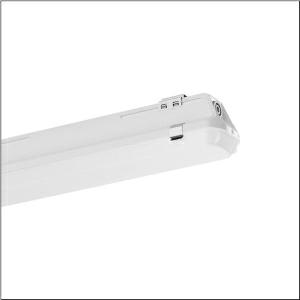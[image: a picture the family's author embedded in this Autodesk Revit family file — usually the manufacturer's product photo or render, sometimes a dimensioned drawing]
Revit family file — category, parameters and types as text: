
# Revit family: monsun_r__11_51fp20dp460h_2810
name_source: partatom
category: Lighting Fixtures
units: mm (PartAtom-declared; Revit-internal decimal feet)

## family parameters
Cut with Voids When Loaded = No
Host = Face
Light Source = No
Part Type = Normal
Room Calculation Point = No
Round Connector Dimension = Use Diameter
Shared = No

## types (1)
- --- (1 x LED, 5450 lm, 34.6 W, 4000K)
    Apparent Load = 35 VA
    CIE Flux Codes = 45 75 93 94 100
    Color Rendering = 80
    Color Temperature = 4000K
    Default Elevation = 1800 mm
    Description = Monsun® 11, damp-proof luminaire, chain hanger, primary optical cover: enclosure, of PC, light emission: direct distribution, primary light characteristic: symmetric, installation type: suspended mounting, surface-mounted, horizontal mounting, vertical mounting, LED, rated luminous flux: 5.450lm, luminous efficacy: 158lm/W, light colour: 840, colour temperature: 4000K, control gear: ECG DALI, with terminal, 5-pole, max. 2.5mm², mains connection: 220..240V, AC, 50/60Hz, rated input power: 35W, luminaire housing, of glass-fibre reinforced polyester, uncoated, bright grey, incl. chain hanger, length: 1.590mm, width: 90mm, height: 88mm, clip for enclosure, of stainless steel (V2A), ceiling mounting element, of stainless steel (V2A), chain hanger, of stainless steel (V2A), protection rating (complete): IP66, insulation class (complete): insulation class I (protective earthing), certification: CE, ENEC, VDE, UKCA, protection symbol: D, impact resistance: IK08, permissible operating ambient temperature: -35..+40°C, standard: EN 50419, EN 60598-2-1, no direct snow, no direct sun, no direct rain, for indoor or canopied outdoor use, corresponds to IFS (International Featured Standards) requirements for safety and quality in the food industry, contact your sales advisor before using the luminaires in applications with unclear chemical exposure, large temperature fluctuations or condensation-forming humidity, LABS conformity tested according to VDMA 24364:2018-05, packaging unit: 1 piece
    Height = 89 mm
    Lamp = 1 x LED
    Lamp Light Flux = 5450 lm
    Lamp Power = 34.6 W
    Lamp count = 1
    Length = 1590 mm
    Luminous efficacy = 158 lm/W
    Manufacturer = Siteco
    ModVariant = No
    Model = 51FP20DP460H
    Mounting Place = Ceiling
    Mounting Type = Surface mounted
    Number of Poles = 1
    OnlyDefault = Yes
    Power Factor = 1
    Product Name = Monsun® 11
    Product group = damp-proof luminaire
    ProductGroupID = 300
    Protection Class = Protection class I
    Protection Degree = IP 66
    RLX_Detail_Level = 1
    RLX_Emergency_Light_Flux = 0 lm
    RLX_Emergency_Type = 0
    RLX_Emergency_Type_DB = No
    RlxData = <blob elided: 92233 chars, md5=03018481>
    Socket = socket
    Standby Power = 0 W
    System Light Flux = 5450 lm
    System Power = 35 W
    Type Comments = factory setting: luminous flux: 100 % | dim-lin: 254 | 232 mA
    Type Image = l_1004748.jpg
    URL = http://relux.com
    VarID = @adj_140609
    Voltage = 0 V
    Weight = 0.00 kg
    Width = 90 mm

## geometry (parser evidence)
native form markers: Blend x4, Sweep x12
no freeform markers — native parametric forms only
